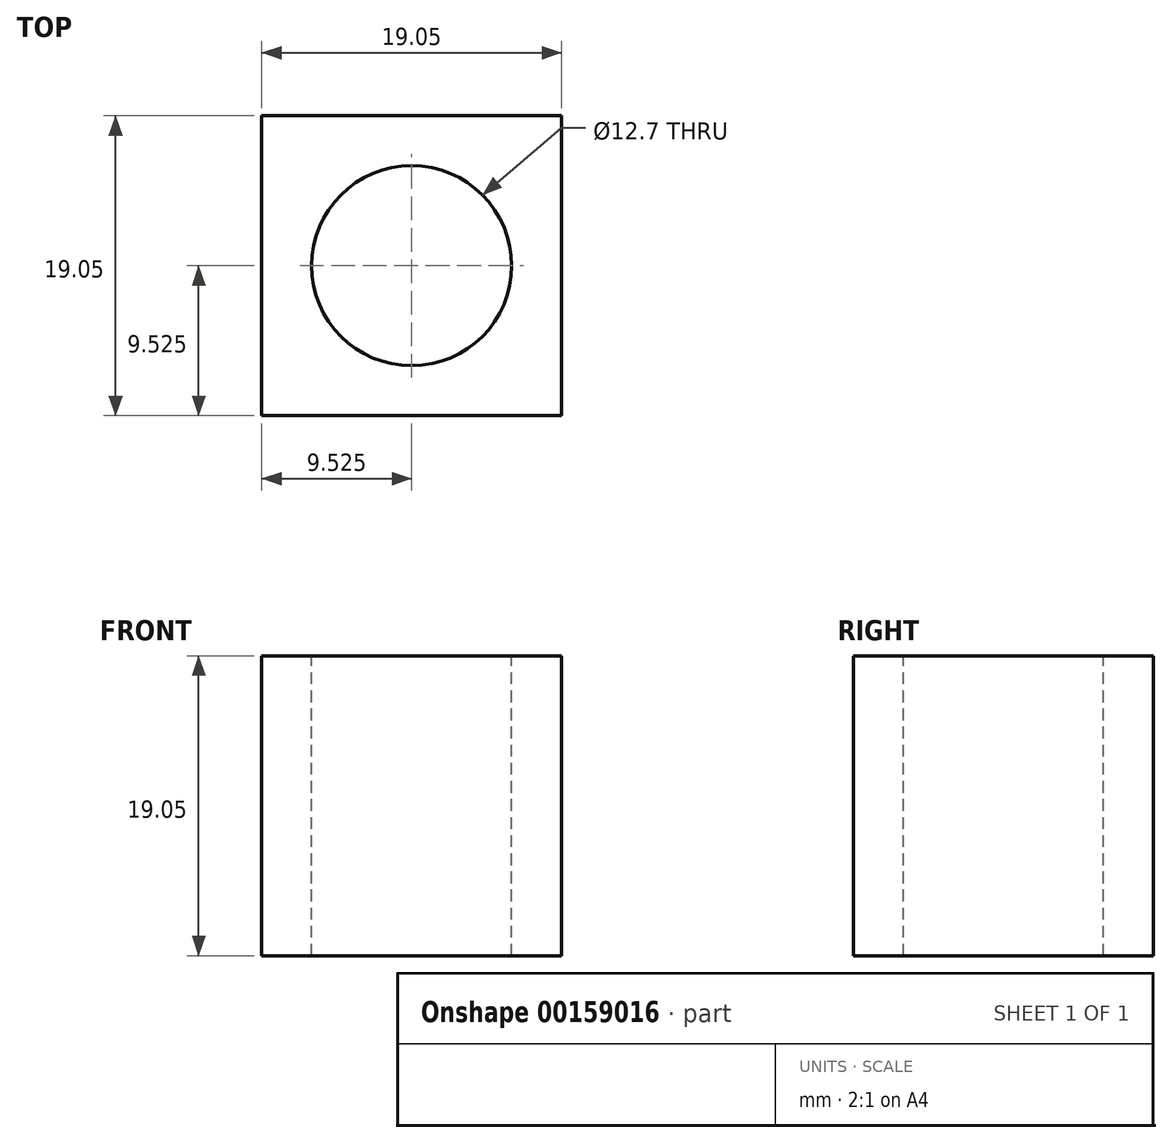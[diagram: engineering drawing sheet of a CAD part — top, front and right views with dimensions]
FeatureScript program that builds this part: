
annotation { "Feature Type Name" : "Feature", "Feature Type Description" : "" }
export const myFeature = defineFeature(function(context is Context, id is Id, definition is map)
    precondition{}
    {
        {
            var Q0;
            Q0=qCreatedBy(makeId("Front.planeOp"),FACE);
            var sketch = newSketch(context, id + "F0", { "sketchPlane" : qUnion([Q0])});
            skLineSegment(sketch, "E0.bottom", {"start": v(0, 0) * mm, "end": v(19.05, 0) * mm});
            skLineSegment(sketch, "E0.top", {"start": v(0, -19.05) * mm, "end": v(19.05, -19.05) * mm});
            skLineSegment(sketch, "E0.left", {"start": v(0, 0) * mm, "end": v(0, -19.05) * mm});
            skLineSegment(sketch, "E0.right", {"start": v(19.05, 0) * mm, "end": v(19.05, -19.05) * mm});
            skSolve(sketch);
        }
        {
            var Q0;
            Q0=makeQuery(id+"F0.imprint","IMPRINT",FACE,{"disambiguationData":[TD([[makeQuery(id+"F0.imprint","IMPRINT",EDGE,{"derivedFrom":sQuery(id+"F0.wireOp",EDGE,"E0.bottom")}),-1.0]])]});
            extrude(context, id + "F1", {"entities" : qUnion([Q0]), "depth" : 19.05 * mm});
        }
        {
            var Q0;
            Q0=makeQuery(id+"F1.opExtrude","SWEPT_FACE",FACE,{"disambiguationData":[OSD([sQuery(id+"F0.wireOp",EDGE,"E0.bottom")])]});
            var sketch = newSketch(context, id + "F2", { "sketchPlane" : qUnion([Q0])});
            skCircle(sketch, "E1", {"center": v(9.53, -9.53) * mm, "radius": 6.35 * mm});
            skPoint(sketch, "E1.centerSnap0", {"position": v(0, -9.53) * mm});
            skPoint(sketch, "E1.centerSnap1", {"position": v(9.53, 0) * mm});
            skSolve(sketch);
        }
        {
            var Q0;
            Q0=makeQuery(id+"F2.imprint","IMPRINT",FACE,{"disambiguationData":[TD([[makeQuery(id+"F2.imprint","IMPRINT",EDGE,{"derivedFrom":sQuery(id+"F2.wireOp",EDGE,"E1")}),1.0]])]});
            extrude(context, id + "F3", {"entities" : qUnion([Q0]), "operationType" : NewBodyOperationType.REMOVE, "oppositeDirection" : true, "depth" : 25.4 * mm});
        }
    });
